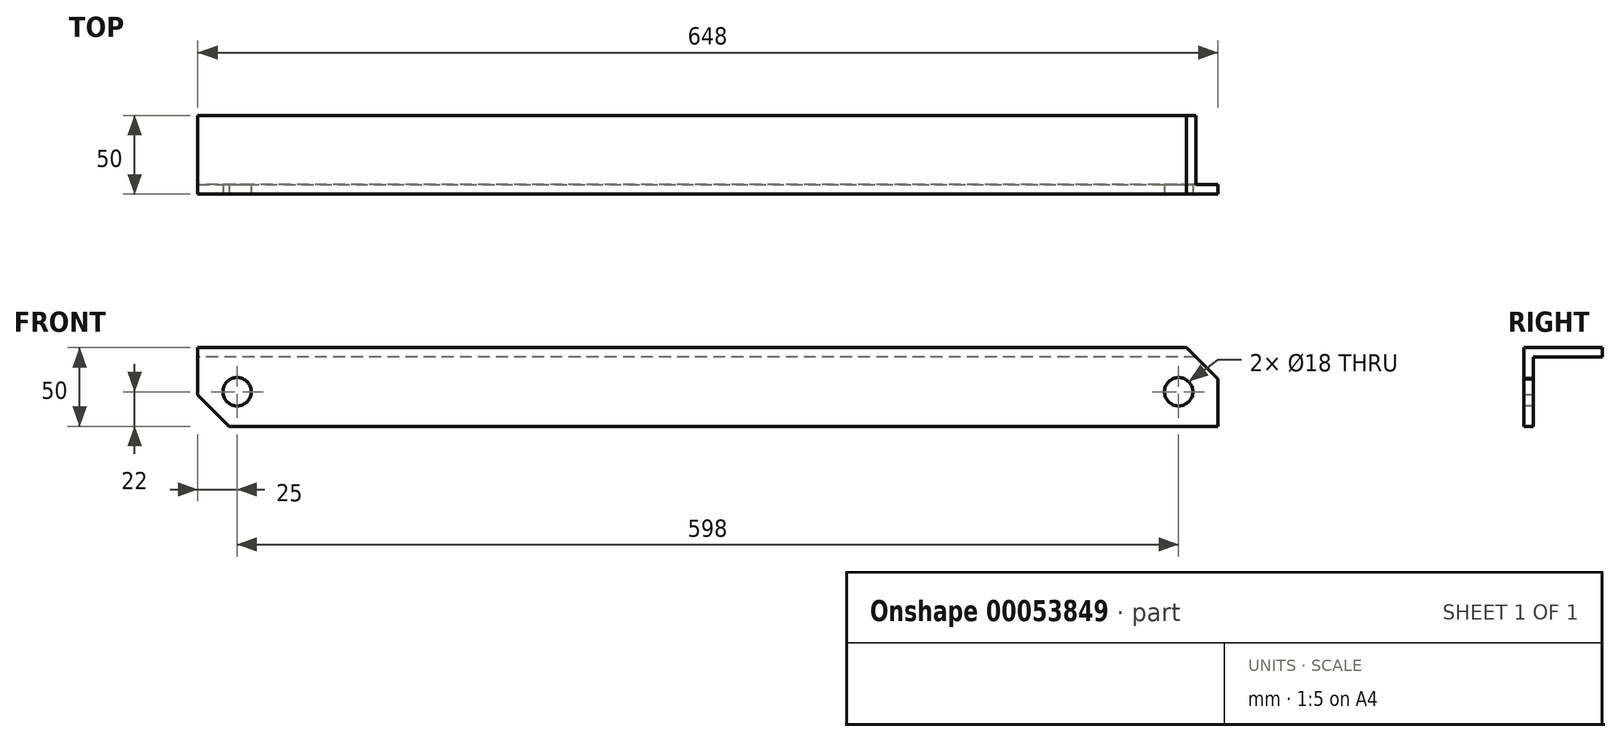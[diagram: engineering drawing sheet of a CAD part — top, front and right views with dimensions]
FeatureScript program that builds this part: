
annotation { "Feature Type Name" : "Feature", "Feature Type Description" : "" }
export const myFeature = defineFeature(function(context is Context, id is Id, definition is map)
    precondition{}
    {
        {
            var Q0;
            Q0=qCreatedBy(makeId("Front.planeOp"),FACE);
            var sketch = newSketch(context, id + "F0", { "sketchPlane" : qUnion([Q0])});
            skLineSegment(sketch, "E0.bottom", {"start": v(0, 0) * mm, "end": v(648, 0) * mm});
            skLineSegment(sketch, "E0.top", {"start": v(0, 50) * mm, "end": v(648, 50) * mm});
            skLineSegment(sketch, "E0.left", {"start": v(0, 0) * mm, "end": v(0, 50) * mm});
            skLineSegment(sketch, "E0.right", {"start": v(648, 0) * mm, "end": v(648, 50) * mm});
            skSolve(sketch);
        }
        {
            var Q0;
            Q0 = qSketchRegion(id + "F0", true);
            extrude(context, id + "F1", {"entities" : qUnion([Q0]), "depth" : 6 * mm});
        }
        {
            var Q0;
            Q0=makeQuery(id+"F1.opExtrude","CAP_FACE",FACE,{"disambiguationData":[OSD([sQuery(id+"F0.wireOp",EDGE,"E0.bottom"),sQuery(id+"F0.wireOp",EDGE,"E0.top"),sQuery(id+"F0.wireOp",EDGE,"E0.left"),sQuery(id+"F0.wireOp",EDGE,"E0.right")])],"isStart":true});
            var sketch = newSketch(context, id + "F2", { "sketchPlane" : qUnion([Q0])});
            skLineSegment(sketch, "E1.bottom", {"start": v(-648, 50) * mm, "end": v(0, 50) * mm});
            skLineSegment(sketch, "E1.top", {"start": v(-648, 44) * mm, "end": v(0, 44) * mm});
            skLineSegment(sketch, "E1.left", {"start": v(-648, 50) * mm, "end": v(-648, 44) * mm});
            skLineSegment(sketch, "E1.right", {"start": v(0, 50) * mm, "end": v(0, 44) * mm});
            skSolve(sketch);
        }
        {
            var Q0;
            Q0 = qSketchRegion(id + "F2", true);
            extrude(context, id + "F3", {"entities" : qUnion([Q0]), "operationType" : NewBodyOperationType.ADD, "depth" : 44 * mm});
        }
        {
            var Q0;
            Q0=makeQuery(id+"F1.opExtrude","CAP_FACE",FACE,{"disambiguationData":[OSD([sQuery(id+"F0.wireOp",EDGE,"E0.bottom"),sQuery(id+"F0.wireOp",EDGE,"E0.top"),sQuery(id+"F0.wireOp",EDGE,"E0.left"),sQuery(id+"F0.wireOp",EDGE,"E0.right")])],"isStart":false});
            var sketch = newSketch(context, id + "F4", { "sketchPlane" : qUnion([Q0])});
            skLineSegment(sketch, "E2", {"start": v(0, 20) * mm, "end": v(20, 0) * mm});
            skLineSegment(sketch, "E3", {"start": v(20, 0) * mm, "end": v(0, 0) * mm});
            skLineSegment(sketch, "E4", {"start": v(0, 0) * mm, "end": v(0, 20) * mm});
            skLineSegment(sketch, "E5", {"start": v(648, 30) * mm, "end": v(628, 50) * mm});
            skLineSegment(sketch, "E6", {"start": v(628, 50) * mm, "end": v(648, 50) * mm});
            skLineSegment(sketch, "E7", {"start": v(648, 50) * mm, "end": v(648, 30) * mm});
            skCircle(sketch, "E8", {"center": v(25, 22) * mm, "radius": 9 * mm});
            skCircle(sketch, "E9", {"center": v(623, 22) * mm, "radius": 9 * mm});
            skSolve(sketch);
        }
        {
            var Q0;
            Q0 = qSketchRegion(id + "F4", true);
            extrude(context, id + "F5", {"entities" : qUnion([Q0]), "operationType" : NewBodyOperationType.REMOVE, "endBound" : BoundingType.THROUGH_ALL, "oppositeDirection" : true, "depth" : 25 * mm});
        }
    });
